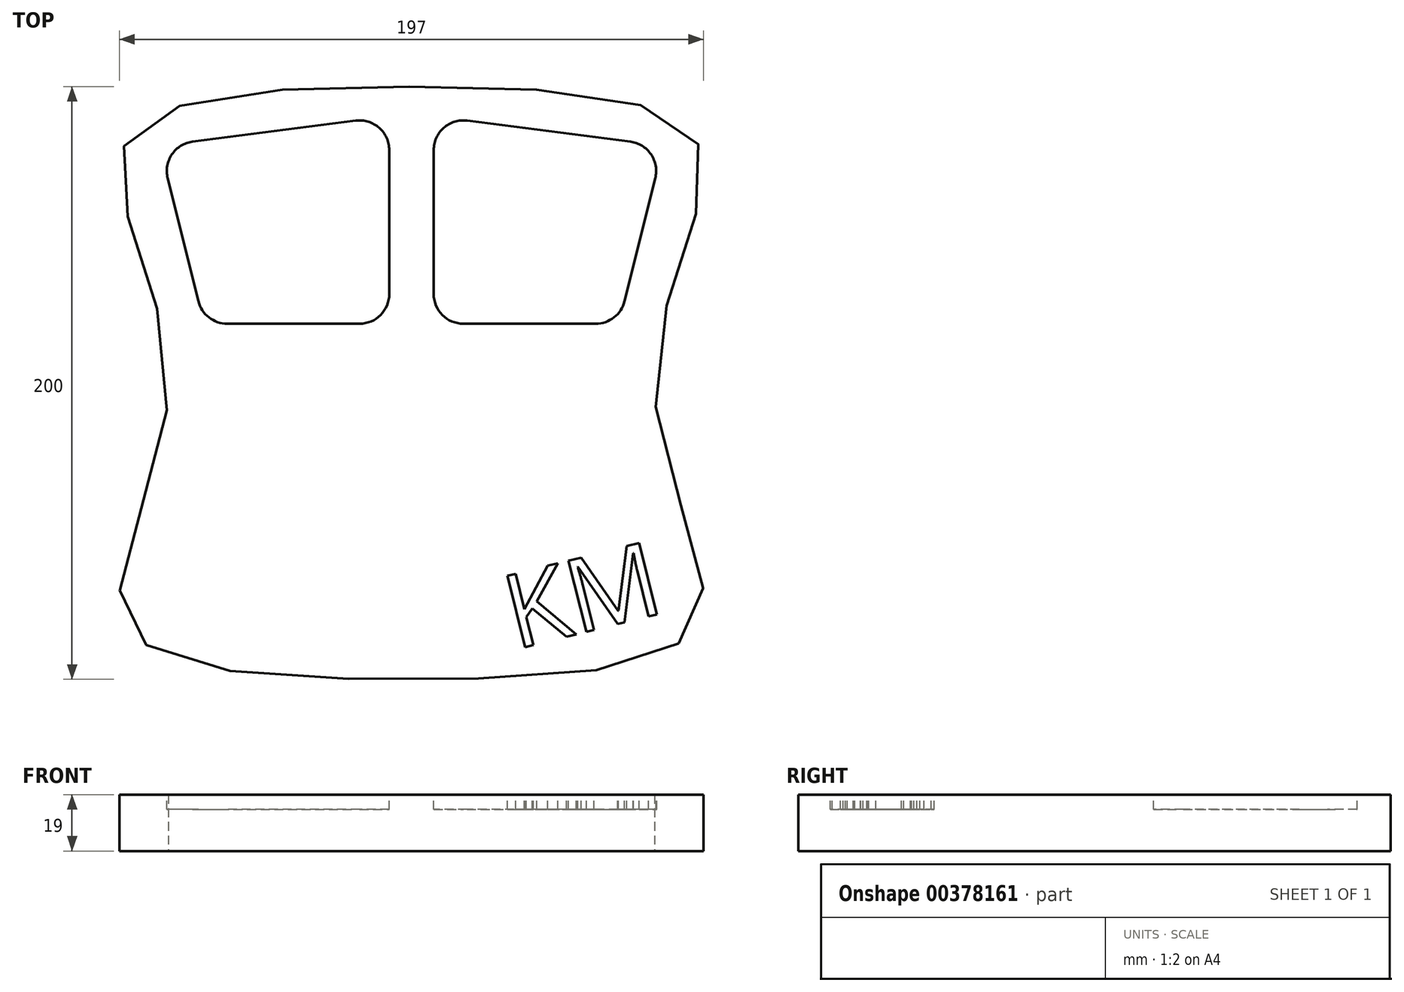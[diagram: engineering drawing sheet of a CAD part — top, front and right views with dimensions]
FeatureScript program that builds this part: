
annotation { "Feature Type Name" : "Feature", "Feature Type Description" : "" }
export const myFeature = defineFeature(function(context is Context, id is Id, definition is map)
    precondition{}
    {
        {
            var Q0;
            Q0=qCreatedBy(makeId("Top.planeOp"),FACE);
            var sketch = newSketch(context, id + "F0", { "sketchPlane" : qUnion([Q0])});
            skLineSegment(sketch, "E0.bottom", {"start": v(0, 0) * mm, "end": v(200, 0) * mm, "construction": true});
            skLineSegment(sketch, "E0.top", {"start": v(0, 200) * mm, "end": v(200, 200) * mm, "construction": true});
            skLineSegment(sketch, "E0.left", {"start": v(0, 0) * mm, "end": v(0, 200) * mm, "construction": true});
            skLineSegment(sketch, "E0.right", {"start": v(200, 0) * mm, "end": v(200, 200) * mm, "construction": true});
            skLineSegment(sketch, "E1.bottom", {"start": v(3, 0) * mm, "end": v(197, 0) * mm, "construction": true});
            skLineSegment(sketch, "E1.top", {"start": v(3, 200) * mm, "end": v(197, 200) * mm, "construction": true});
            skLineSegment(sketch, "E1.left", {"start": v(3, 0) * mm, "end": v(3, 200) * mm, "construction": true});
            skLineSegment(sketch, "E1.right", {"start": v(197, 0) * mm, "end": v(197, 200) * mm, "construction": true});
            skFitSpline(sketch, "E2", {"points": [v(3, 180) * mm, v(100, 200) * mm, v(197, 180) * mm, v(182, 100) * mm, v(197, 20) * mm, v(100, 0) * mm, v(3, 20) * mm, v(18, 100) * mm, v(3, 180) * mm]});
            skSolve(sketch);
        }
        {
            var Q0;
            Q0 = qSketchRegion(id + "F0", true);
            extrude(context, id + "F1", {"entities" : qUnion([Q0]), "depth" : 19 * mm});
        }
        {
            var Q0;
            Q0=makeQuery(id+"F1.opExtrude","CAP_FACE",FACE,{"disambiguationData":[OSD([sQuery(id+"F0.wireOp",EDGE,"E2")])],"isStart":false});
            var sketch = newSketch(context, id + "F2", { "sketchPlane" : qUnion([Q0])});
            skText(sketch, "E3", { "text": "KM", "fontName": "OpenSans-Regular.ttf"});
            skLineSegment(sketch, "E4.bottom", {"start": v(0, 0) * mm, "end": v(200, 0) * mm, "construction": true});
            skLineSegment(sketch, "E4.top", {"start": v(0, 200) * mm, "end": v(200, 200) * mm, "construction": true});
            skLineSegment(sketch, "E4.left", {"start": v(0, 0) * mm, "end": v(0, 200) * mm, "construction": true});
            skLineSegment(sketch, "E4.right", {"start": v(200, 0) * mm, "end": v(200, 200) * mm, "construction": true});
            skLineSegment(sketch, "E5", {"start": v(92.5, 178.63) * mm, "end": v(92.5, 130) * mm});
            skLineSegment(sketch, "E6", {"start": v(82.5, 120) * mm, "end": v(37.8, 120) * mm});
            skLineSegment(sketch, "E7", {"start": v(28.1, 127.57) * mm, "end": v(17.73, 169.1) * mm});
            skLineSegment(sketch, "E8", {"start": v(26.15, 181.44) * mm, "end": v(81.22, 188.54) * mm});
            skLineSegment(sketch, "E9", {"start": v(107.5, 130) * mm, "end": v(107.5, 178.63) * mm});
            skLineSegment(sketch, "E10", {"start": v(118.78, 188.54) * mm, "end": v(173.85, 181.44) * mm});
            skLineSegment(sketch, "E11", {"start": v(182.27, 169.1) * mm, "end": v(171.9, 127.57) * mm});
            skLineSegment(sketch, "E12", {"start": v(162.2, 120) * mm, "end": v(117.5, 120) * mm});
            skPoint(sketch, "E13.visualSharp", {"position": v(15, 180) * mm});
            skArc(sketch, "E13.filletArc", {"start": v(26.15, 181.44) * mm, "mid": v(19.17, 177.16) * mm, "end": v(17.73, 169.1) * mm});
            skPoint(sketch, "E14.visualSharp", {"position": v(185, 180) * mm});
            skArc(sketch, "E14.filletArc", {"start": v(182.27, 169.1) * mm, "mid": v(180.83, 177.16) * mm, "end": v(173.85, 181.44) * mm});
            skPoint(sketch, "E15.visualSharp", {"position": v(107.5, 190) * mm});
            skArc(sketch, "E15.filletArc", {"start": v(118.78, 188.54) * mm, "mid": v(110.9, 186.14) * mm, "end": v(107.5, 178.63) * mm});
            skPoint(sketch, "E16.visualSharp", {"position": v(92.5, 190) * mm});
            skArc(sketch, "E16.filletArc", {"start": v(92.5, 178.63) * mm, "mid": v(89.1, 186.14) * mm, "end": v(81.22, 188.54) * mm});
            skPoint(sketch, "E17.visualSharp", {"position": v(30, 120) * mm});
            skArc(sketch, "E17.filletArc", {"start": v(28.1, 127.57) * mm, "mid": v(31.65, 122.12) * mm, "end": v(37.8, 120) * mm});
            skPoint(sketch, "E18.visualSharp", {"position": v(92.5, 120) * mm});
            skArc(sketch, "E18.filletArc", {"start": v(82.5, 120) * mm, "mid": v(89.57, 122.93) * mm, "end": v(92.5, 130) * mm});
            skPoint(sketch, "E19.visualSharp", {"position": v(107.5, 120) * mm});
            skArc(sketch, "E19.filletArc", {"start": v(107.5, 130) * mm, "mid": v(110.43, 122.93) * mm, "end": v(117.5, 120) * mm});
            skPoint(sketch, "E20.visualSharp", {"position": v(170, 120) * mm});
            skArc(sketch, "E20.filletArc", {"start": v(162.2, 120) * mm, "mid": v(168.35, 122.12) * mm, "end": v(171.9, 127.57) * mm});
            const initialGuessF2  = {"E3": [0.135, 0.01, 0.97051, 0.24105, 0.025]};
            skSetInitialGuess(sketch, initialGuessF2);
            skSolve(sketch);
        }
        {
            var Q0;
            Q0 = qSketchRegion(id + "F2", true);
            extrude(context, id + "F3", {"entities" : qUnion([Q0]), "operationType" : NewBodyOperationType.REMOVE, "oppositeDirection" : true, "depth" : 5 * mm});
        }
    });
